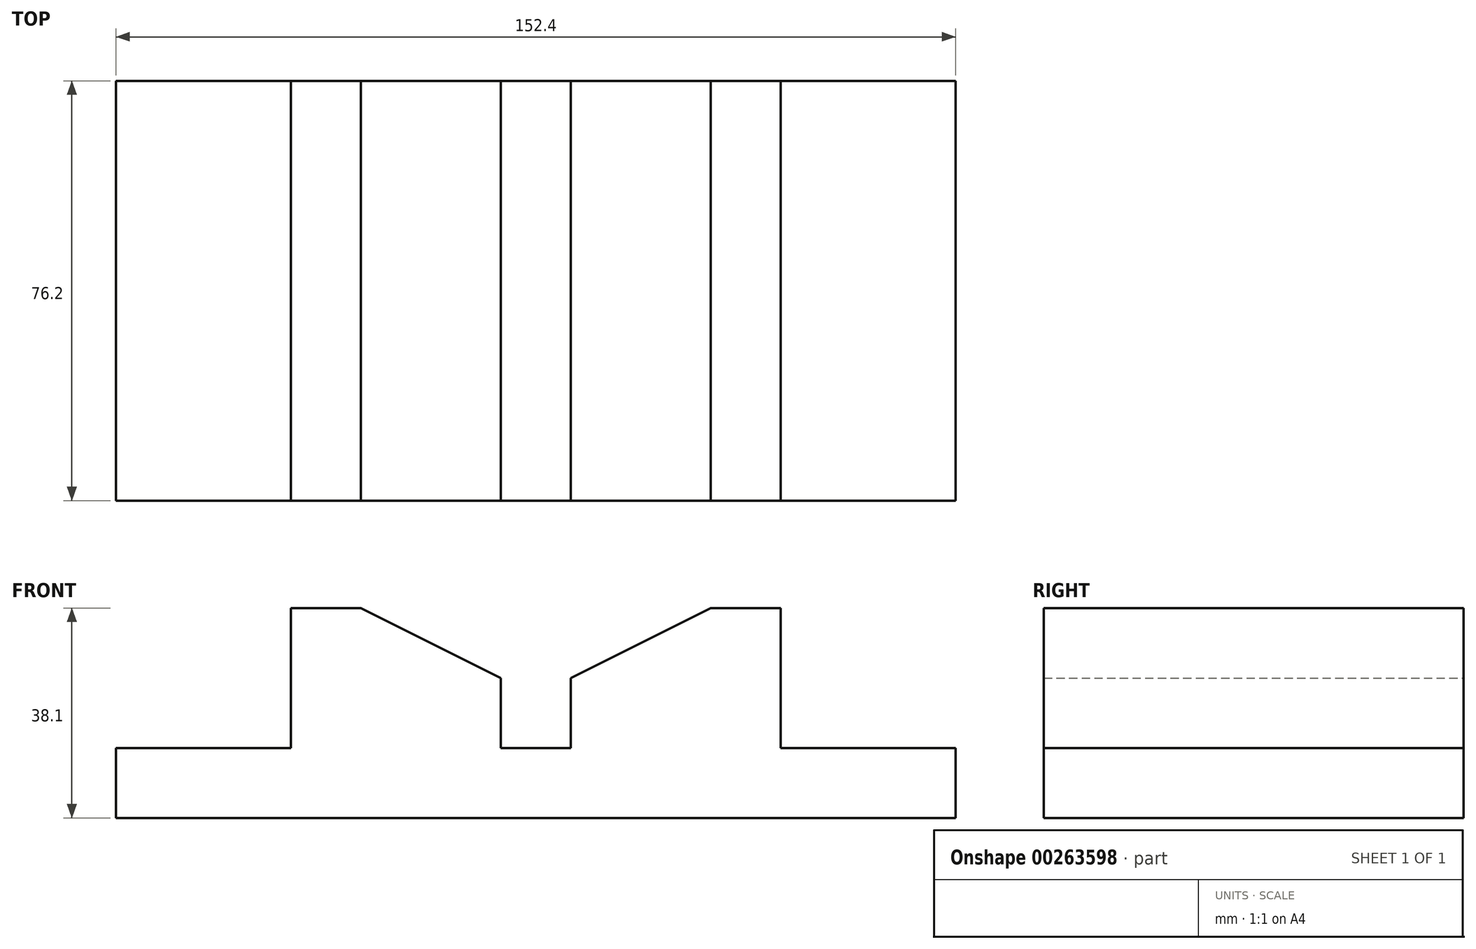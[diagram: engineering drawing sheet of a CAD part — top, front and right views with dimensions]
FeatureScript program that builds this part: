
annotation { "Feature Type Name" : "Feature", "Feature Type Description" : "" }
export const myFeature = defineFeature(function(context is Context, id is Id, definition is map)
    precondition{}
    {
        {
            var Q0;
            Q0=qCreatedBy(makeId("Front.planeOp"),FACE);
            var sketch = newSketch(context, id + "F0", { "sketchPlane" : qUnion([Q0])});
            skLineSegment(sketch, "E0", {"start": v(-75.7, 0) * mm, "end": v(76.7, 0) * mm});
            skLineSegment(sketch, "E1", {"start": v(-75.7, 0) * mm, "end": v(-75.7, 12.7) * mm});
            skLineSegment(sketch, "E2", {"start": v(-75.7, 12.7) * mm, "end": v(-43.94, 12.7) * mm});
            skLineSegment(sketch, "E3", {"start": v(-43.94, 12.7) * mm, "end": v(-43.94, 38.1) * mm});
            skLineSegment(sketch, "E4", {"start": v(-43.94, 38.1) * mm, "end": v(-31.24, 38.1) * mm});
            skLineSegment(sketch, "E5", {"start": v(-5.84, 12.7) * mm, "end": v(-5.84, 25.4) * mm});
            skLineSegment(sketch, "E6", {"start": v(-31.24, 38.1) * mm, "end": v(-5.84, 25.4) * mm});
            skLineSegment(sketch, "E7", {"start": v(-5.84, 12.7) * mm, "end": v(6.86, 12.7) * mm});
            skLineSegment(sketch, "E8", {"start": v(6.86, 12.7) * mm, "end": v(6.86, 25.4) * mm});
            skLineSegment(sketch, "E9", {"start": v(76.7, 0) * mm, "end": v(76.7, 12.7) * mm});
            skLineSegment(sketch, "E10", {"start": v(76.7, 12.7) * mm, "end": v(44.96, 12.7) * mm});
            skLineSegment(sketch, "E11", {"start": v(44.96, 12.7) * mm, "end": v(44.96, 38.1) * mm});
            skLineSegment(sketch, "E12", {"start": v(44.96, 38.1) * mm, "end": v(32.26, 38.1) * mm});
            skLineSegment(sketch, "E13", {"start": v(32.26, 38.1) * mm, "end": v(6.86, 25.4) * mm});
            skSolve(sketch);
        }
        {
            var Q0;
            Q0 = qSketchRegion(id + "F0", true);
            extrude(context, id + "F1", {"entities" : qUnion([Q0]), "depth" : 76.2 * mm});
        }
    });
